# Revit family: S-797
name_source: partatom
category: Plumbing Fixtures
revit_build: Autodesk Revit 2015 (Build: 20140606_1530(x64)
units: mm (PartAtom-declared; Revit-internal decimal feet)

## types (2) — shared parameters
Description = TRIANGULAR FLOOR GULLY FOR CORNER TILED SHOWERS, ORIENTABLE TRAP, HORIZONTAL OUTLET, WITH GRID DROPS, HEIGHT REGULATION
Dmax = 26 mm
Dmin = 10 mm  [stored 0.0328084 ft]
E = 40 mm  [stored 0.131234 ft]
F = 50 mm  [stored 0.164042 ft]
Flowrate = 0.8 L/s
Grid = INOX AISI304
Hidraulic seal = 50 mm
Hmax = 16 mm  [stored 0.0524934 ft]
Hmin = 6 mm  [stored 0.019685 ft]
Manufacturer = Jimten
Material = ABS
Model = S-797
Size = 236mm x 331mm x 236 mm
Total Minimum Height = 115-125mm
Type Comments = WITH WALL FIXATION, WITH PRESSING RING FOR WATERPROOFING PVC OR GEOTEXTILE MEMBRANES. WITH PROTECTION COVER.  WITH GRID HEIGHT ADJUSTABLE.
URL = http://www.jimten.com
WFU = 1

## per-type parameters (varying)
| type | Outlet | Reference |
| S-797_40_DROPS | 40H | 13374 |
| S-797_40-50_DROPS | 40M/50M | 13375 |

note: [stored X ft] marks values corroborated as IEEE doubles in the binary element streams (Revit-internal decimal feet)

## geometry (parser evidence)
native form markers: Blend x3, Sweep x18
no freeform markers — native parametric forms only
